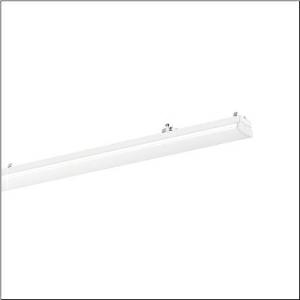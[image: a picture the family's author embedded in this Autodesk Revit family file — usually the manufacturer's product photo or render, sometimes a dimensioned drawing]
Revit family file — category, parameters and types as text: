
# Revit family: licross_11_recessed_opal_mo_51te1dmn46xg
name_source: partatom
category: Lighting Fixtures
units: mm (PartAtom-declared; Revit-internal decimal feet)

## family parameters
Cut with Voids When Loaded = No
Host = Face
Light Source = No
Part Type = Normal
Room Calculation Point = No
Round Connector Dimension = Use Diameter
Shared = No

## types (1)
- --- (1 x LED, 6320 lm, 34.3 W, 4000K)
    Apparent Load = 34 VA
    CIE Flux Codes = 44 73 91 87 100
    Color Rendering = 80
    Color Temperature = 4000K
    Default Elevation = 1800 mm
    Description = Licross 11 recessed opal MO, luminaire insert, of sheet steel, coil coated, white, length: 1.500mm, width: 76mm, height: 87mm, LED rated luminous flux: 4.320lm, light colour: 840, SDCM (Standard Deviation of Colour Matching)MacAdam ≤ 2 SDCM (initial), control gear: ON/OFF Multilumen, with plug, 3-pole, with phase selection, mains connection: 220..240V, AC, 50/60Hz, rated input power: 34W, internal wiring halogen-free, primary optical cover: cover, of PMMA, light emission: direct with ceiling illumination distribution, primary light characteristic: symmetric, protection rating (complete): IP54, insulation class (complete): insulation class I (protective earthing), certification: CE, ENEC, VDE, UKCA, protection symbol: D if used in an environment with non-conductive dust loads with corresponding accessories, impact resistance: IK06, permissible ambient temperature for indoor applications: -35..+50°C, corresponds to IFS (International Featured Standards) requirements for safety and quality in the food industry, reducing of maximum allowable ambient temperature of 5°C with ceiling mounting, The light source and the operating device comply with the requirements of the Ecodesign Regulation (EU) 2019/2020 and are replaceable in accordance with this regulation, packaging unit: 1 piece
    Height = 83 mm
    Lamp = 1 x LED
    Lamp Light Flux = 6320 lm
    Lamp Power = 34.3 W
    Lamp count = 1
    Length = 1500 mm
    Luminous efficacy = 184 lm/W
    Manufacturer = Siteco
    ModVariant = No
    Model = 51TE1DMN46XG
    Mounting Place = Ceiling
    Mounting Type = Pendant
    Number of Poles = 1
    OnlyDefault = Yes
    Power Factor = 1
    Product Name = Licross 11 recessed opal MO
    Product group = luminaire insert | ceiling pendant
    ProductGroupID = 901
    Protection Class = Protection class I
    Protection Degree = IP 54
    RLX_Detail_Level = 1
    RLX_Emergency_Light_Flux = 0 lm
    RLX_Emergency_Type = 0
    RLX_Emergency_Type_DB = No
    RlxData = <blob elided: 24829 chars, md5=dd3f5fcc>
    Socket = socket
    Standby Power = 0 W
    System Light Flux = 6320 lm
    System Power = 34 W
    Type Comments = factory setting: luminous flux: 100 % | (A | C | E) | 79 mA
    Type Image = l_1313666.jpg
    URL = http://relux.com
    VarID = @adj_070735
    Voltage = 0 V
    Weight = 0.00 kg
    Width = 76 mm

## geometry (parser evidence)
native form markers: Blend x4, Sweep x13
no freeform markers — native parametric forms only
